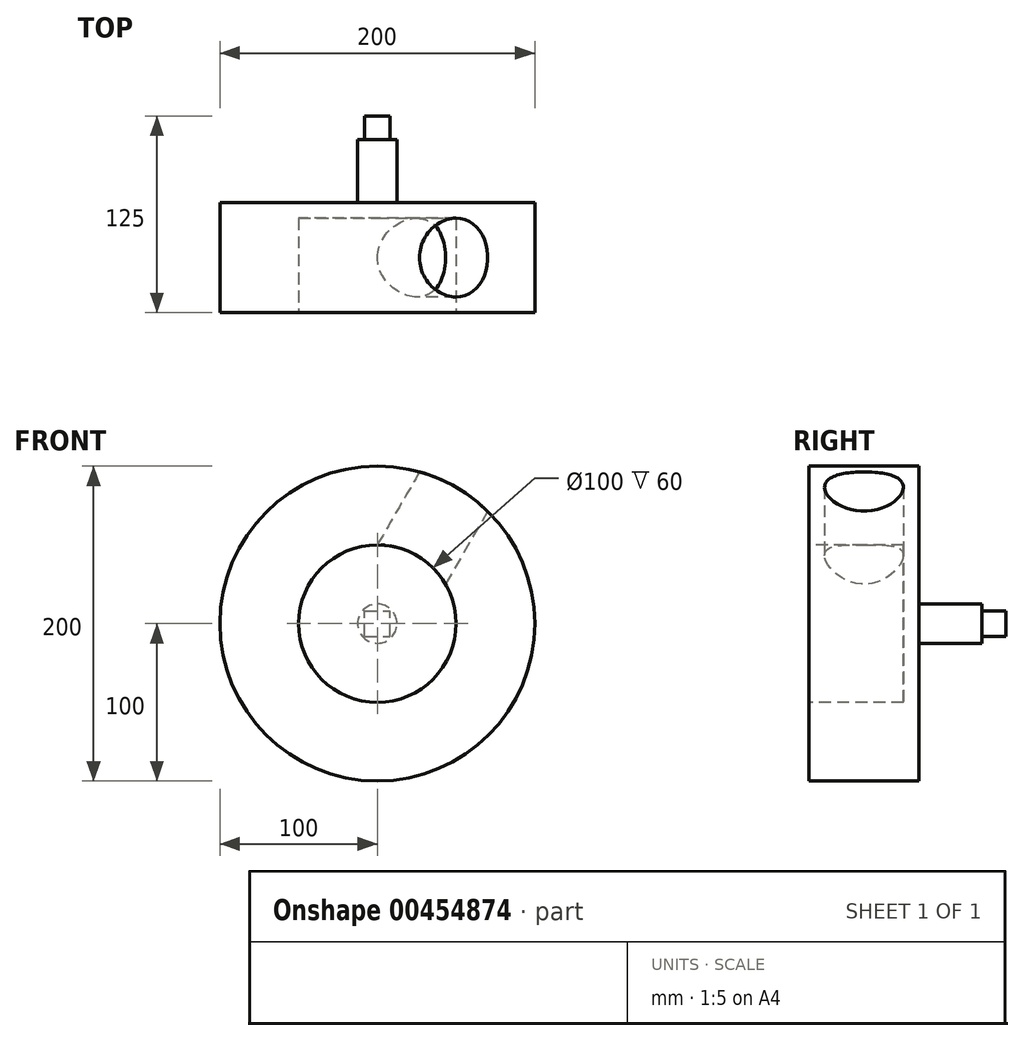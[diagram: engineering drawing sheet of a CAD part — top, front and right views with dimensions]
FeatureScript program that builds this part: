
annotation { "Feature Type Name" : "Feature", "Feature Type Description" : "" }
export const myFeature = defineFeature(function(context is Context, id is Id, definition is map)
    precondition{}
    {
        {
            var Q0;
            Q0=qCreatedBy(makeId("Front.planeOp"),FACE);
            var sketch = newSketch(context, id + "F0", { "sketchPlane" : qUnion([Q0])});
            skCircle(sketch, "E0", {"center": v(0, 0) * mm, "radius": 100 * mm});
            skSolve(sketch);
        }
        {
            var Q0;
            Q0 = qSketchRegion(id + "F0", true);
            extrude(context, id + "F1", {"entities" : qUnion([Q0]), "depth" : 70 * mm, "symmetric" : true});
        }
        {
            var Q0;
            Q0=makeQuery(id+"F1.opExtrude","CAP_FACE",FACE,{"disambiguationData":[OSD([sQuery(id+"F0.wireOp",EDGE,"E0")])],"isStart":false});
            var sketch = newSketch(context, id + "F2", { "sketchPlane" : qUnion([Q0])});
            skCircle(sketch, "E1", {"center": v(0, 0) * mm, "radius": 50 * mm});
            skSolve(sketch);
        }
        {
            var Q0;
            Q0=makeQuery(id+"F2.imprint","IMPRINT",FACE,{"disambiguationData":[TD([[makeQuery(id+"F2.imprint","IMPRINT",EDGE,{"derivedFrom":sQuery(id+"F2.wireOp",EDGE,"E1")}),1.0]])]});
            extrude(context, id + "F3", {"entities" : qUnion([Q0]), "operationType" : NewBodyOperationType.REMOVE, "oppositeDirection" : true, "depth" : 60 * mm});
        }
        {
            var Q0;
            Q0=makeQuery(id+"F1.opExtrude","CAP_FACE",FACE,{"disambiguationData":[OSD([sQuery(id+"F0.wireOp",EDGE,"E0")])],"isStart":true});
            var sketch = newSketch(context, id + "F4", { "sketchPlane" : qUnion([Q0])});
            skCircle(sketch, "E2", {"center": v(0, 0) * mm, "radius": 12.5 * mm});
            skSolve(sketch);
        }
        {
            var Q0;
            Q0=makeQuery(id+"F4.imprint","IMPRINT",FACE,{"disambiguationData":[TD([[makeQuery(id+"F4.imprint","IMPRINT",EDGE,{"derivedFrom":sQuery(id+"F4.wireOp",EDGE,"E2")}),1.0]])]});
            extrude(context, id + "F5", {"entities" : qUnion([Q0]), "operationType" : NewBodyOperationType.ADD, "depth" : 40 * mm});
        }
        {
            var Q0;
            Q0=makeQuery(id+"F5.opExtrude","CAP_FACE",FACE,{"disambiguationData":[OSD([sQuery(id+"F4.wireOp",EDGE,"E2")])],"isStart":false});
            var sketch = newSketch(context, id + "F6", { "sketchPlane" : qUnion([Q0])});
            skLineSegment(sketch, "E3.bottom", {"start": v(8, -8) * mm, "end": v(-8, -8) * mm});
            skLineSegment(sketch, "E3.top", {"start": v(8, 8) * mm, "end": v(-8, 8) * mm});
            skLineSegment(sketch, "E3.left", {"start": v(8, -8) * mm, "end": v(8, 8) * mm});
            skLineSegment(sketch, "E3.right", {"start": v(-8, -8) * mm, "end": v(-8, 8) * mm});
            skPoint(sketch, "E3.middle", {"position": v(0, 0) * mm});
            skSolve(sketch);
        }
        {
            var Q0;
            Q0=makeQuery(id+"F6.imprint","IMPRINT",FACE,{"disambiguationData":[TD([[makeQuery(id+"F6.imprint","IMPRINT",EDGE,{"derivedFrom":sQuery(id+"F6.wireOp",EDGE,"E3.bottom")}),-1.0]])]});
            extrude(context, id + "F7", {"entities" : qUnion([Q0]), "operationType" : NewBodyOperationType.ADD, "depth" : 15 * mm});
        }
        {
            var Q0;
            Q0=qCreatedBy(makeId("Top.planeOp"),FACE);
            var sketch = newSketch(context, id + "F8", { "sketchPlane" : qUnion([Q0])});
            skLineSegment(sketch, "E4", {"start": v(0, 110.63) * mm, "end": v(0, -75.56) * mm, "construction": true});
            skSolve(sketch);
        }
        {
            var Q0;
            Q0=qCreatedBy(makeId("Top.planeOp"),FACE);
            var Q1;
            Q1=sQuery(id+"F8.wireOp",EDGE,"E4");
            cPlane(context, id + "F9", {"entities" : qUnion([Q0, Q1]), "cplaneType" : CPlaneType.LINE_ANGLE, "offset" : 25 * mm, "angle" : 150 * degree, "width" : 150 * mm, "height" : 150 * mm});
        }
        {
            var Q0;
            Q0=qCreatedBy(id+"F9.planeOp",FACE);
            var sketch = newSketch(context, id + "F10", { "sketchPlane" : qUnion([Q0])});
            skCircle(sketch, "E5", {"center": v(0, 0) * mm, "radius": 25 * mm});
            skLineSegment(sketch, "E6.0", {"start": v(50, 25) * mm, "end": v(-50, 25) * mm, "construction": true});
            skSolve(sketch);
        }
        {
            var Q0;
            Q0=makeQuery(id+"F10.imprint","IMPRINT",FACE,{"disambiguationData":[TD([[makeQuery(id+"F10.imprint","IMPRINT",EDGE,{"derivedFrom":sQuery(id+"F10.wireOp",EDGE,"E5")}),1.0]])]});
            extrude(context, id + "F11", {"entities" : qUnion([Q0]), "operationType" : NewBodyOperationType.REMOVE, "endBound" : BoundingType.THROUGH_ALL, "depth" : 25 * mm});
        }
    });
